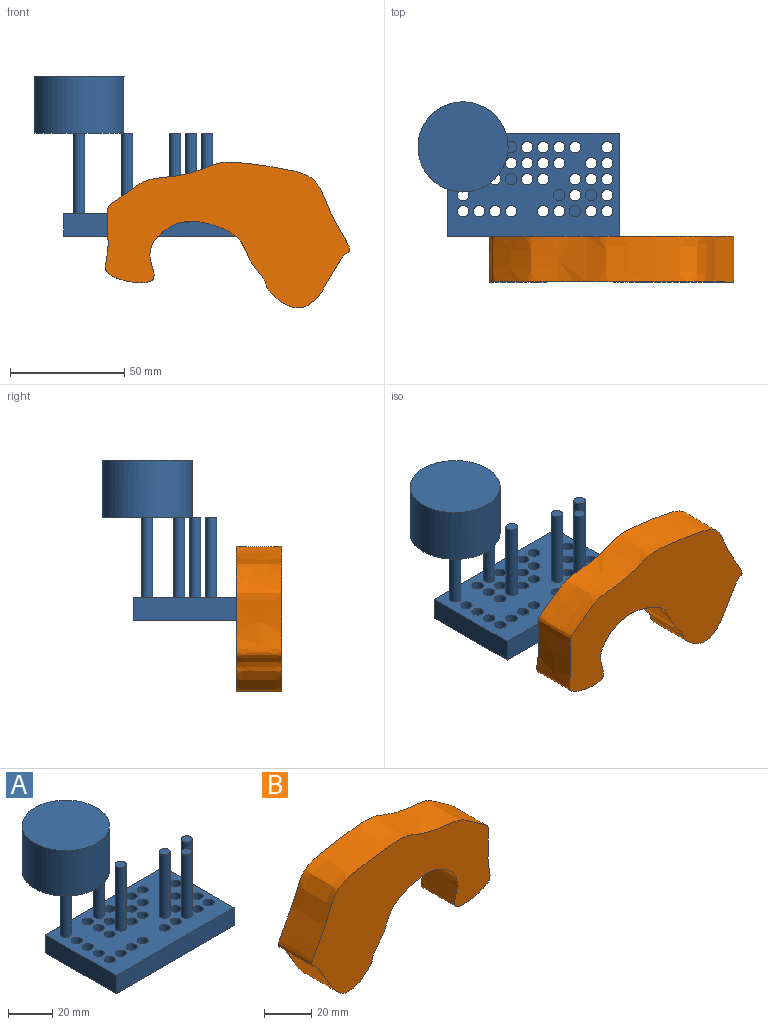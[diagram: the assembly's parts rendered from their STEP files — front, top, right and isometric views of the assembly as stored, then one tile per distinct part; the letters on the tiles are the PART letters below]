
ASSEMBLY  parts=2 mates=1
PART A: 52 faces, bbox 87.9x58.7x70 mm
  f0: plane 45x10mm, normal (1,0,0), area 450mm2, adj f1,f35,f36,f37
  f1: plane 75x10mm, normal (0,1,0), area 750mm2, adj f0,f2,f36,f37
  f2: plane 45x10mm, normal (-1,0,0), area 450mm2, adj f1,f35,f36,f37
  f3: cylinder r=2.5mm len=10mm, axis (0,0,-1), area 157.1mm2, adj f36,f37
  f4: cylinder r=2.5mm len=10mm, axis (0,0,-1), area 157.1mm2, adj f36,f37
  f5: cylinder r=2.5mm len=10mm, axis (0,0,-1), area 157.1mm2, adj f36,f37
  f6: cylinder r=2.5mm len=10mm, axis (0,0,-1), area 157.1mm2, adj f36,f37
  f7: cylinder r=2.5mm len=10mm, axis (0,0,-1), area 157.1mm2, adj f36,f37
  f8: cylinder r=2.5mm len=10mm, axis (0,0,-1), area 157.1mm2, adj f36,f37
  f9: cylinder r=2.5mm len=10mm, axis (0,0,-1), area 157.1mm2, adj f36,f37
  f10: cylinder r=2.5mm len=10mm, axis (0,0,-1), area 157.1mm2, adj f36,f37
  f11: cylinder r=2.5mm len=10mm, axis (0,0,-1), area 157.1mm2, adj f36,f37
  f12: cylinder r=2.5mm len=10mm, axis (0,0,-1), area 157.1mm2, adj f36,f37
  f13: cylinder r=2.5mm len=10mm, axis (0,0,-1), area 157.1mm2, adj f36,f37
  f14: cylinder r=2.5mm len=10mm, axis (0,0,-1), area 157.1mm2, adj f36,f37
  f15: cylinder r=2.5mm len=10mm, axis (0,0,-1), area 157.1mm2, adj f36,f37
  f16: cylinder r=2.5mm len=10mm, axis (0,0,-1), area 157.1mm2, adj f36,f37
  f17: cylinder r=2.5mm len=10mm, axis (0,0,-1), area 157.1mm2, adj f36,f37
  f18: cylinder r=2.5mm len=10mm, axis (0,0,-1), area 157.1mm2, adj f36,f37
  f19: cylinder r=2.5mm len=10mm, axis (0,0,-1), area 157.1mm2, adj f36,f37
  f20: cylinder r=2.5mm len=10mm, axis (0,0,-1), area 157.1mm2, adj f36,f37
  f21: cylinder r=2.5mm len=10mm, axis (0,0,-1), area 157.1mm2, adj f36,f37
  f22: cylinder r=2.5mm len=10mm, axis (0,0,-1), area 157.1mm2, adj f36,f37
  f23: cylinder r=2.5mm len=10mm, axis (0,0,-1), area 157.1mm2, adj f36,f37
  f24: cylinder r=2.5mm len=10mm, axis (0,0,-1), area 157.1mm2, adj f36,f37
  f25: cylinder r=2.5mm len=10mm, axis (0,0,-1), area 157.1mm2, adj f36,f37
  f26: cylinder r=2.5mm len=10mm, axis (0,0,-1), area 157.1mm2, adj f36,f37
  f27: cylinder r=2.5mm len=10mm, axis (0,0,-1), area 157.1mm2, adj f36,f37
  f28: cylinder r=2.5mm len=10mm, axis (0,0,-1), area 157.1mm2, adj f36,f37
  f29: cylinder r=2.5mm len=10mm, axis (0,0,-1), area 157.1mm2, adj f36,f37
  f30: cylinder r=2.5mm len=10mm, axis (0,0,-1), area 157.1mm2, adj f36,f37
  f31: cylinder r=2.5mm len=10mm, axis (0,0,-1), area 157.1mm2, adj f36,f37
  f32: cylinder r=2.5mm len=10mm, axis (0,0,-1), area 157.1mm2, adj f36,f37
  f33: cylinder r=2.5mm len=10mm, axis (0,0,-1), area 157.1mm2, adj f36,f37
  f34: cylinder r=2.5mm len=10mm, axis (0,0,-1), area 157.1mm2, adj f36,f37
  f35: plane 75x10mm, normal (0,-1,0), area 750mm2, adj f0,f2,f36,f37
  f36: plane 75x45mm, normal (0,0,1), area 2628.9mm2, adj f0,f1,f2,f3,f4,f5,f6,f7
  f37: plane 75x45mm, normal (0,0,-1), area 2746.7mm2, adj f0,f1,f2,f3,f4,f5,f6,f7
  f38: cylinder r=2.5mm len=35mm, axis (0,0,-1), area 549.8mm2, adj f36,f49
  f39: cylinder r=2.5mm len=35mm, axis (0,0,-1), area 549.8mm2, adj f36,f40,f49
  f40: plane 5x3.91mm, normal (0,0,1), area 16.2mm2, adj f39,f50
  f41: cylinder r=2.5mm len=35mm, axis (0,0,-1), area 549.8mm2, adj f36,f42
  f42: plane 5x5mm, normal (0,0,1), area 19.6mm2, adj f41
  f43: cylinder r=2.5mm len=35mm, axis (0,0,-1), area 549.8mm2, adj f36,f44
  f44: plane 5x5mm, normal (0,0,1), area 19.6mm2, adj f43
  f45: cylinder r=2.5mm len=35mm, axis (0,0,-1), area 549.8mm2, adj f36,f46
  f46: plane 5x5mm, normal (0,0,1), area 19.6mm2, adj f45
  f47: cylinder r=2.5mm len=35mm, axis (0,0,-1), area 549.8mm2, adj f36,f48
  f48: plane 5x5mm, normal (0,0,1), area 19.6mm2, adj f47
  f49: plane 39.39x39.29mm, normal (0,0,-1), area 1195.8mm2, adj f38,f39,f50
  f50: cylinder r=19.7mm len=39.39mm, axis (0,0,-1), area 3094mm2, adj f40,f49,f51
  f51: plane 39.39x39.39mm, normal (0,0,1), area 1218.8mm2, adj f50
PART B: 3 faces, bbox 109.4x20x66.1 mm
  f0: extruded ~106.79x63.37mm, area 6338.5mm2, adj f1,f2
  f1: plane 109.37x66.06mm, normal (0,-1,0), area 3834.4mm2, adj f0
  f2: plane 109.37x66.06mm, normal (0,1,0), area 3834.4mm2, adj f0
PLACE A t=(-9.89,8.56,2.26)mm
PLACE B rot(axis=(0,0,-1),180deg) t=(15.55,-33.94,-4.02)mm
MATE fastened B.f1 <-> A.f35  axis (0,1,0) through (27.61,-13.94,7.26)mm
